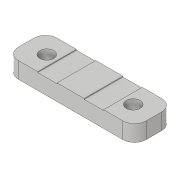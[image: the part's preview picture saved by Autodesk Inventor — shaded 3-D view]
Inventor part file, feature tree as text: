
AUTODESK INVENTOR PART (.ipt)
format: ipt  version: 2020 (Build 240168000, 168)  size: 262,144 bytes
history: native  units: in
note: dims shown in document units (in); Inventor stores cm internally (conversion verified against a paired STEP export)
features: extrude x5, sketch x5, mirror x2, plane x1, fillet x1
ambient origin geometry x8: Origin, YZ Plane, XZ Plane, XY Plane, X Axis, Y Axis, Z Axis, Center Point
bodies: Solid1 (feature_tree)
feature tree (14):
  extrude  "Extrusion1"  Depth=0.3937in
  extrude  "Extrusion2"  Depth=0.1575in TaperAngle=0.0deg
  plane  "Work Plane1"
  mirror  "Mirror1"
  fillet  "Fillet1"  [1 undecoded]
  extrude  "Extrusion3"  Depth=0.1417in
  extrude  "Extrusion4"  Depth=0.3937in
  mirror  "Mirror2"
  extrude  "Extrusion5"  Depth=0.315in
  sketch  "Sketch1"  dims[d0=1.2992in d1=0.3937in]
  sketch  "Sketch2"  dims[d2=0.1575in d3=0.0in d5=0.1575in d6=0.0in d7=-0.6496in]
  sketch  "Sketch3"  dims[d8=0.1181in d9=0.1417in]
  sketch  "Sketch4"  dims[d10=0.2756in d11=0.3937in]
  sketch  "Sketch5"  dims[d12=0.0079in d13=0.0in d14=0.315in d15=0.3937in d16=0.1181in d17=0.0079in d18=0.0in d19=0.0197in d20=0.0in]
note: 1 required parameter value undecoded (feature->parameter linkage not recoverable at this tier; creation-order binding heuristic only, values carry confidence <= 0.55)
